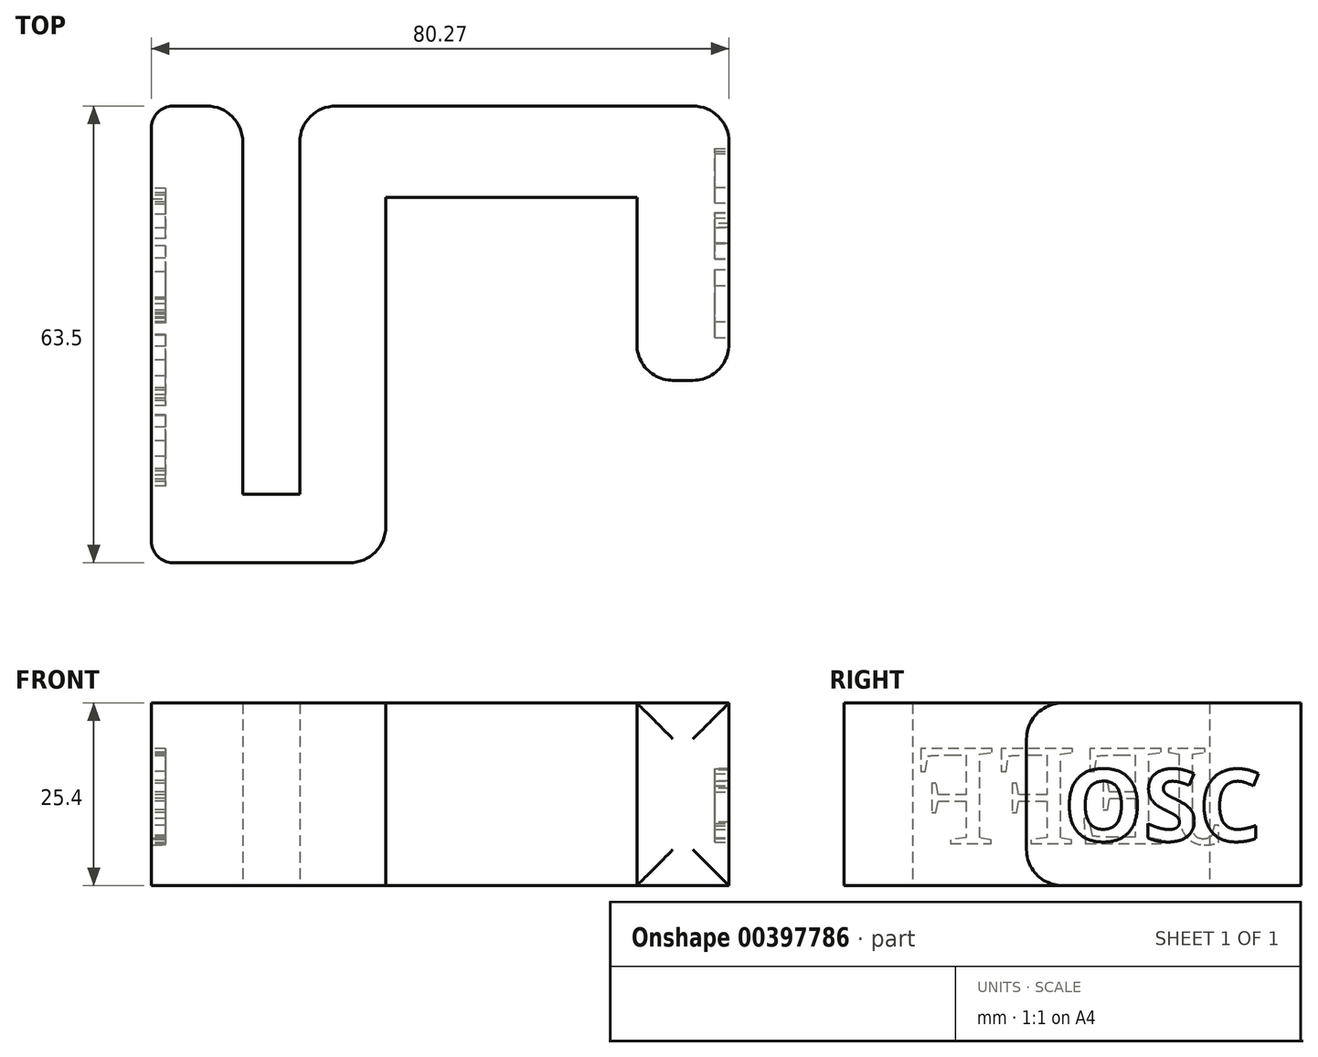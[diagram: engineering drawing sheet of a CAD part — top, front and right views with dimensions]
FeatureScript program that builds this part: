
annotation { "Feature Type Name" : "Feature", "Feature Type Description" : "" }
export const myFeature = defineFeature(function(context is Context, id is Id, definition is map)
    precondition{}
    {
        {
            var Q0;
            Q0=qCreatedBy(makeId("Top.planeOp"),FACE);
            var sketch = newSketch(context, id + "F0", { "sketchPlane" : qUnion([Q0])});
            skLineSegment(sketch, "E0", {"start": v(0, 0) * mm, "end": v(0, 63.5) * mm});
            skLineSegment(sketch, "E1", {"start": v(0, 63.5) * mm, "end": v(12.7, 63.5) * mm});
            skLineSegment(sketch, "E2", {"start": v(12.7, 63.5) * mm, "end": v(12.7, 9.53) * mm});
            skLineSegment(sketch, "E3", {"start": v(12.7, 9.53) * mm, "end": v(20.64, 9.53) * mm});
            skLineSegment(sketch, "E4", {"start": v(20.64, 9.53) * mm, "end": v(20.64, 63.5) * mm});
            skLineSegment(sketch, "E5", {"start": v(20.64, 63.5) * mm, "end": v(80.27, 63.5) * mm});
            skLineSegment(sketch, "E6", {"start": v(80.27, 63.5) * mm, "end": v(80.27, 25.35) * mm});
            skLineSegment(sketch, "E7", {"start": v(80.27, 25.35) * mm, "end": v(67.48, 25.35) * mm});
            skLineSegment(sketch, "E8", {"start": v(67.48, 25.35) * mm, "end": v(67.48, 50.8) * mm});
            skLineSegment(sketch, "E9", {"start": v(67.48, 50.8) * mm, "end": v(32.58, 50.8) * mm});
            skLineSegment(sketch, "E10", {"start": v(32.58, 50.8) * mm, "end": v(32.58, 0) * mm});
            skLineSegment(sketch, "E11", {"start": v(32.58, 0) * mm, "end": v(0, 0) * mm});
            skSolve(sketch);
        }
        {
            var Q0;
            Q0=makeQuery(id+"F0.imprint","IMPRINT",FACE,{"disambiguationData":[TD([[makeQuery(id+"F0.imprint","IMPRINT",EDGE,{"derivedFrom":sQuery(id+"F0.wireOp",EDGE,"E0")}),-1.0]])]});
            extrude(context, id + "F1", {"entities" : qUnion([Q0]), "depth" : 25.4 * mm});
        }
        {
            var Q0;
            Q0=makeQuery(id+"F1.opExtrude","CAP_EDGE",EDGE,{"disambiguationData":[OSD([sQuery(id+"F0.wireOp",EDGE,"E7")])],"isStart":false});
            var Q1;
            Q1=makeQuery(id+"F1.opExtrude","CAP_EDGE",EDGE,{"disambiguationData":[OSD([sQuery(id+"F0.wireOp",EDGE,"E7")])],"isStart":true});
            var Q2;
            Q2=makeQuery(id+"F1.opExtrude","SWEPT_EDGE",EDGE,{"disambiguationData":[OSD([sQuery(id+"F0.wireOp",EDGE,"E6"),sQuery(id+"F0.wireOp",EDGE,"E7")])]});
            var Q3;
            Q3=makeQuery(id+"F1.opExtrude","SWEPT_EDGE",EDGE,{"disambiguationData":[OSD([sQuery(id+"F0.wireOp",EDGE,"E7"),sQuery(id+"F0.wireOp",EDGE,"E8")])]});
            var Q4;
            Q4=makeQuery(id+"F1.opExtrude","SWEPT_EDGE",EDGE,{"disambiguationData":[OSD([sQuery(id+"F0.wireOp",EDGE,"E5"),sQuery(id+"F0.wireOp",EDGE,"E6")])]});
            var Q5;
            Q5=makeQuery(id+"F1.opExtrude","SWEPT_EDGE",EDGE,{"disambiguationData":[OSD([sQuery(id+"F0.wireOp",EDGE,"E10"),sQuery(id+"F0.wireOp",EDGE,"E11")])]});
            var Q6;
            Q6=makeQuery(id+"F1.opExtrude","SWEPT_EDGE",EDGE,{"disambiguationData":[OSD([sQuery(id+"F0.wireOp",EDGE,"E4"),sQuery(id+"F0.wireOp",EDGE,"E5")])]});
            var Q7;
            Q7=makeQuery(id+"F1.opExtrude","SWEPT_EDGE",EDGE,{"disambiguationData":[OSD([sQuery(id+"F0.wireOp",EDGE,"E1"),sQuery(id+"F0.wireOp",EDGE,"E2")])]});
            fillet(context, id + "F2", {"entities" : qUnion([Q0, Q1, Q2, Q3, Q4, Q5, Q6, Q7]), "radius" : 5 * mm, "tangentPropagation" : true, "allowEdgeOverflow" : false});
        }
        {
            var Q0;
            Q0=makeQuery(id+"F1.opExtrude","SWEPT_FACE",FACE,{"disambiguationData":[OSD([sQuery(id+"F0.wireOp",EDGE,"E0")])]});
            var sketch = newSketch(context, id + "F3", { "sketchPlane" : qUnion([Q0])});
            skText(sketch, "E12", { "text": "JEFF", "fontName": "Tinos-Regular.ttf"});
            const initialGuessF3  = {"E12": [-0.05248, 0.00586, 1, 0, 0.0145]};
            skSetInitialGuess(sketch, initialGuessF3);
            skSolve(sketch);
        }
        {
            var Q0;
            Q0 = qSketchRegion(id + "F3", true);
            extrude(context, id + "F4", {"entities" : qUnion([Q0]), "operationType" : NewBodyOperationType.REMOVE, "oppositeDirection" : true, "depth" : 2 * mm, "offsetDistance" : 25 * mm});
        }
        {
            var Q0;
            Q0=makeQuery(id+"F1.opExtrude","SWEPT_FACE",FACE,{"disambiguationData":[OSD([sQuery(id+"F0.wireOp",EDGE,"E6")])]});
            var sketch = newSketch(context, id + "F5", { "sketchPlane" : qUnion([Q0])});
            skText(sketch, "E13", { "text": "OSC", "fontName": "OpenSans-Bold.ttf"});
            const initialGuessF5  = {"E13": [0.0305, 0.0062, 1, 0, 0.01001]};
            skSetInitialGuess(sketch, initialGuessF5);
            skSolve(sketch);
        }
        {
            var Q0;
            Q0 = qSketchRegion(id + "F5", true);
            extrude(context, id + "F6", {"entities" : qUnion([Q0]), "operationType" : NewBodyOperationType.REMOVE, "oppositeDirection" : true, "depth" : 2 * mm, "offsetDistance" : 25 * mm});
        }
        {
            var Q0;
            Q0=makeQuery(id+"F1.opExtrude","SWEPT_EDGE",EDGE,{"disambiguationData":[OSD([sQuery(id+"F0.wireOp",EDGE,"E0"),sQuery(id+"F0.wireOp",EDGE,"E11")])]});
            var Q1;
            Q1=makeQuery(id+"F1.opExtrude","SWEPT_EDGE",EDGE,{"disambiguationData":[OSD([sQuery(id+"F0.wireOp",EDGE,"E0"),sQuery(id+"F0.wireOp",EDGE,"E1")])]});
            fillet(context, id + "F7", {"entities" : qUnion([Q0, Q1]), "radius" : 3 * mm, "tangentPropagation" : true, "allowEdgeOverflow" : false});
        }
    });
